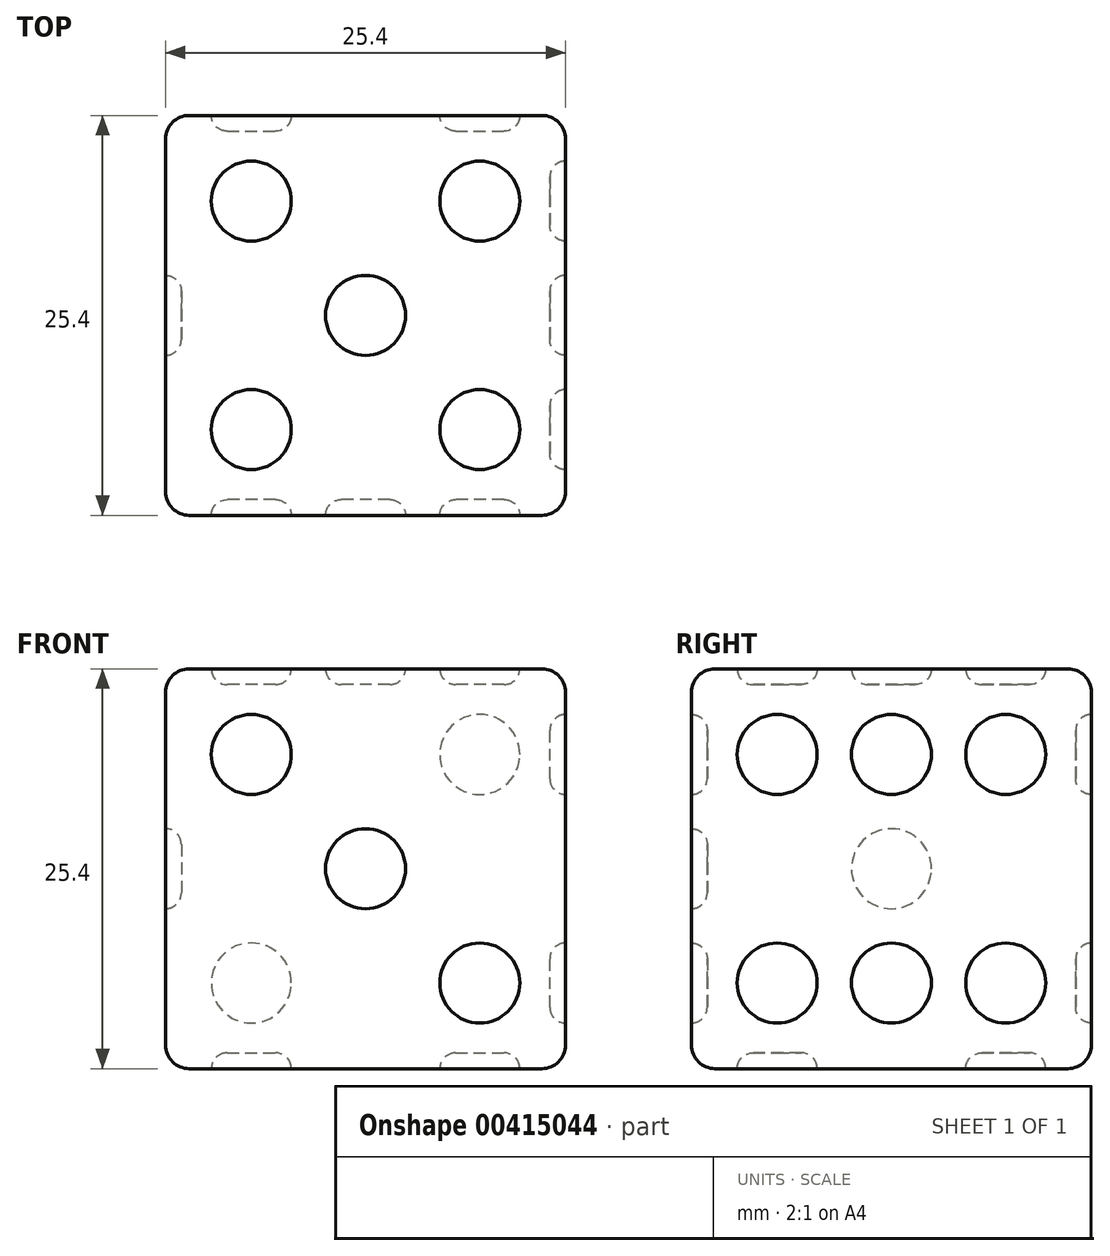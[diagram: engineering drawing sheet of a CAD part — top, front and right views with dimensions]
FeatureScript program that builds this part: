
annotation { "Feature Type Name" : "Feature", "Feature Type Description" : "" }
export const myFeature = defineFeature(function(context is Context, id is Id, definition is map)
    precondition{}
    {
        {
            assignVariable(context, id + "F0", {"name" : "size", "anyValue" : 25.4});
        }
        {
            assignVariable(context, id + "F1", {"name" : "radius", "anyValue" : 1.5});
        }
        {
            var Q0;
            Q0=qCreatedBy(makeId("Top.planeOp"),FACE);
            var sketch = newSketch(context, id + "F2", { "sketchPlane" : qUnion([Q0])});
            skLineSegment(sketch, "E0.bottom", {"start": v(12.7, -12.7) * mm, "end": v(-12.7, -12.7) * mm});
            skLineSegment(sketch, "E0.top", {"start": v(12.7, 12.7) * mm, "end": v(-12.7, 12.7) * mm});
            skLineSegment(sketch, "E0.left", {"start": v(12.7, -12.7) * mm, "end": v(12.7, 12.7) * mm});
            skLineSegment(sketch, "E0.right", {"start": v(-12.7, -12.7) * mm, "end": v(-12.7, 12.7) * mm});
            skPoint(sketch, "E0.middle", {"position": v(0, 0) * mm});
            skSolve(sketch);
        }
        {
            var Q0;
            Q0=makeQuery(id+"F2.imprint","IMPRINT",FACE,{"disambiguationData":[TD([[makeQuery(id+"F2.imprint","IMPRINT",EDGE,{"derivedFrom":sQuery(id+"F2.wireOp",EDGE,"E0.bottom")}),-1.0]])]});
            extrude(context, id + "F3", {"entities" : qUnion([Q0]), "depth" : (getVariable(context, 'size')) * mm});
        }
        {
            var Q0;
            Q0=makeQuery(id+"F3.opExtrude","CAP_FACE",FACE,{"disambiguationData":[OSD([sQuery(id+"F2.wireOp",EDGE,"E0.bottom"),sQuery(id+"F2.wireOp",EDGE,"E0.top"),sQuery(id+"F2.wireOp",EDGE,"E0.left"),sQuery(id+"F2.wireOp",EDGE,"E0.right")])],"isStart":true});
            var sketch = newSketch(context, id + "F4", { "sketchPlane" : qUnion([Q0])});
            skPoint(sketch, "E1", {"position": v(0, 0) * mm});
            skPoint(sketch, "E2", {"position": v(0, 7.26) * mm});
            skPoint(sketch, "E3", {"position": v(7.26, 7.26) * mm});
            skPoint(sketch, "E4", {"position": v(7.26, 0) * mm});
            skPoint(sketch, "E5", {"position": v(7.26, -7.26) * mm});
            skPoint(sketch, "E6", {"position": v(0, -7.26) * mm});
            skPoint(sketch, "E7", {"position": v(-7.26, -7.26) * mm});
            skPoint(sketch, "E8", {"position": v(-7.26, 0) * mm});
            skPoint(sketch, "E9", {"position": v(-7.26, 7.26) * mm});
            skLineSegment(sketch, "E10", {"start": v(-7.26, 7.26) * mm, "end": v(0, 7.26) * mm, "construction": true});
            skLineSegment(sketch, "E11", {"start": v(7.26, 7.26) * mm, "end": v(7.26, 0) * mm, "construction": true});
            skLineSegment(sketch, "E12", {"start": v(7.26, 0) * mm, "end": v(7.26, -7.26) * mm, "construction": true});
            skLineSegment(sketch, "E13", {"start": v(7.26, -7.26) * mm, "end": v(0, -7.26) * mm, "construction": true});
            skLineSegment(sketch, "E14", {"start": v(0, -7.26) * mm, "end": v(-7.26, -7.26) * mm, "construction": true});
            skLineSegment(sketch, "E15", {"start": v(-7.26, 0) * mm, "end": v(-7.26, -7.26) * mm, "construction": true});
            skLineSegment(sketch, "E16", {"start": v(-7.26, 0) * mm, "end": v(-7.26, 7.26) * mm, "construction": true});
            skLineSegment(sketch, "E17", {"start": v(0, 7.26) * mm, "end": v(7.26, 7.26) * mm, "construction": true});
            skLineSegment(sketch, "E18", {"start": v(0, 7.26) * mm, "end": v(0, 0) * mm, "construction": true});
            skLineSegment(sketch, "E19", {"start": v(0, 0) * mm, "end": v(0, -7.26) * mm, "construction": true});
            skLineSegment(sketch, "E20", {"start": v(0, 0) * mm, "end": v(7.26, 0) * mm, "construction": true});
            skLineSegment(sketch, "E21", {"start": v(0, 0) * mm, "end": v(-7.26, 0) * mm, "construction": true});
            skCircle(sketch, "E22", {"center": v(-7.26, 7.26) * mm, "radius": 2.54 * mm});
            skCircle(sketch, "E23", {"center": v(-7.26, 0) * mm, "radius": 2.54 * mm});
            skCircle(sketch, "E24", {"center": v(-7.26, -7.26) * mm, "radius": 2.54 * mm});
            skCircle(sketch, "E25", {"center": v(0, -7.26) * mm, "radius": 2.54 * mm});
            skCircle(sketch, "E26", {"center": v(7.26, -7.26) * mm, "radius": 2.54 * mm});
            skCircle(sketch, "E27", {"center": v(7.26, 0) * mm, "radius": 2.54 * mm});
            skCircle(sketch, "E28", {"center": v(7.26, 7.26) * mm, "radius": 2.54 * mm});
            skCircle(sketch, "E29", {"center": v(0, 0) * mm, "radius": 2.54 * mm});
            skCircle(sketch, "E30", {"center": v(0, 7.26) * mm, "radius": 2.54 * mm});
            skSolve(sketch);
        }
        {
            var Q0;
            Q0=makeQuery(id+"F3.opExtrude","CAP_FACE",FACE,{"disambiguationData":[OSD([sQuery(id+"F2.wireOp",EDGE,"E0.bottom"),sQuery(id+"F2.wireOp",EDGE,"E0.top"),sQuery(id+"F2.wireOp",EDGE,"E0.left"),sQuery(id+"F2.wireOp",EDGE,"E0.right")])],"isStart":false});
            var sketch = newSketch(context, id + "F5", { "sketchPlane" : qUnion([Q0])});
            skPoint(sketch, "E31", {"position": v(0, 0) * mm});
            skPoint(sketch, "E32", {"position": v(0, 7.26) * mm});
            skPoint(sketch, "E33", {"position": v(7.26, 7.26) * mm});
            skPoint(sketch, "E34", {"position": v(7.26, 0) * mm});
            skPoint(sketch, "E35", {"position": v(7.26, -7.26) * mm});
            skPoint(sketch, "E36", {"position": v(0, -7.26) * mm});
            skPoint(sketch, "E37", {"position": v(-7.26, -7.26) * mm});
            skPoint(sketch, "E38", {"position": v(-7.26, 0) * mm});
            skPoint(sketch, "E39", {"position": v(-7.26, 7.26) * mm});
            skLineSegment(sketch, "E40", {"start": v(-7.26, 7.26) * mm, "end": v(0, 7.26) * mm, "construction": true});
            skLineSegment(sketch, "E41", {"start": v(7.26, 7.26) * mm, "end": v(7.26, 0) * mm, "construction": true});
            skLineSegment(sketch, "E42", {"start": v(7.26, 0) * mm, "end": v(7.26, -7.26) * mm, "construction": true});
            skLineSegment(sketch, "E43", {"start": v(7.26, -7.26) * mm, "end": v(0, -7.26) * mm, "construction": true});
            skLineSegment(sketch, "E44", {"start": v(0, -7.26) * mm, "end": v(-7.26, -7.26) * mm, "construction": true});
            skLineSegment(sketch, "E45", {"start": v(-7.26, 0) * mm, "end": v(-7.26, -7.26) * mm, "construction": true});
            skLineSegment(sketch, "E46", {"start": v(-7.26, 0) * mm, "end": v(-7.26, 7.26) * mm, "construction": true});
            skLineSegment(sketch, "E47", {"start": v(0, 7.26) * mm, "end": v(7.26, 7.26) * mm, "construction": true});
            skLineSegment(sketch, "E48", {"start": v(0, 7.26) * mm, "end": v(0, 0) * mm, "construction": true});
            skLineSegment(sketch, "E49", {"start": v(0, 0) * mm, "end": v(0, -7.26) * mm, "construction": true});
            skLineSegment(sketch, "E50", {"start": v(0, 0) * mm, "end": v(7.26, 0) * mm, "construction": true});
            skLineSegment(sketch, "E51", {"start": v(0, 0) * mm, "end": v(-7.26, 0) * mm, "construction": true});
            skCircle(sketch, "E52", {"center": v(-7.26, 7.26) * mm, "radius": 2.54 * mm});
            skCircle(sketch, "E53", {"center": v(-7.26, 0) * mm, "radius": 2.54 * mm});
            skCircle(sketch, "E54", {"center": v(-7.26, -7.26) * mm, "radius": 2.54 * mm});
            skCircle(sketch, "E55", {"center": v(0, -7.26) * mm, "radius": 2.54 * mm});
            skCircle(sketch, "E56", {"center": v(7.26, -7.26) * mm, "radius": 2.54 * mm});
            skCircle(sketch, "E57", {"center": v(7.26, 0) * mm, "radius": 2.54 * mm});
            skCircle(sketch, "E58", {"center": v(7.26, 7.26) * mm, "radius": 2.54 * mm});
            skCircle(sketch, "E59", {"center": v(0, 0) * mm, "radius": 2.54 * mm});
            skCircle(sketch, "E60", {"center": v(0, 7.26) * mm, "radius": 2.54 * mm});
            skSolve(sketch);
        }
        {
            var Q0;
            Q0=makeQuery(id+"F3.opExtrude","SWEPT_FACE",FACE,{"disambiguationData":[OSD([sQuery(id+"F2.wireOp",EDGE,"E0.left")])]});
            var sketch = newSketch(context, id + "F6", { "sketchPlane" : qUnion([Q0])});
            skPoint(sketch, "E61", {"position": v(0, 12.7) * mm});
            skPoint(sketch, "E62", {"position": v(0, 19.96) * mm});
            skPoint(sketch, "E63", {"position": v(7.26, 19.96) * mm});
            skPoint(sketch, "E64", {"position": v(7.26, 12.7) * mm});
            skPoint(sketch, "E65", {"position": v(7.26, 5.44) * mm});
            skPoint(sketch, "E66", {"position": v(0, 5.44) * mm});
            skPoint(sketch, "E67", {"position": v(-7.26, 5.44) * mm});
            skPoint(sketch, "E68", {"position": v(-7.26, 12.7) * mm});
            skPoint(sketch, "E69", {"position": v(-7.26, 19.96) * mm});
            skLineSegment(sketch, "E70", {"start": v(-7.26, 19.96) * mm, "end": v(0, 19.96) * mm, "construction": true});
            skLineSegment(sketch, "E71", {"start": v(7.26, 19.96) * mm, "end": v(7.26, 12.7) * mm, "construction": true});
            skLineSegment(sketch, "E72", {"start": v(7.26, 12.7) * mm, "end": v(7.26, 5.44) * mm, "construction": true});
            skLineSegment(sketch, "E73", {"start": v(7.26, 5.44) * mm, "end": v(0, 5.44) * mm, "construction": true});
            skLineSegment(sketch, "E74", {"start": v(0, 5.44) * mm, "end": v(-7.26, 5.44) * mm, "construction": true});
            skLineSegment(sketch, "E75", {"start": v(-7.26, 12.7) * mm, "end": v(-7.26, 5.44) * mm, "construction": true});
            skLineSegment(sketch, "E76", {"start": v(-7.26, 12.7) * mm, "end": v(-7.26, 19.96) * mm, "construction": true});
            skLineSegment(sketch, "E77", {"start": v(0, 19.96) * mm, "end": v(7.26, 19.96) * mm, "construction": true});
            skLineSegment(sketch, "E78", {"start": v(0, 19.96) * mm, "end": v(0, 12.7) * mm, "construction": true});
            skLineSegment(sketch, "E79", {"start": v(0, 12.7) * mm, "end": v(0, 5.44) * mm, "construction": true});
            skLineSegment(sketch, "E80", {"start": v(0, 12.7) * mm, "end": v(7.26, 12.7) * mm, "construction": true});
            skLineSegment(sketch, "E81", {"start": v(0, 12.7) * mm, "end": v(-7.26, 12.7) * mm, "construction": true});
            skCircle(sketch, "E82", {"center": v(-7.26, 19.96) * mm, "radius": 2.54 * mm});
            skCircle(sketch, "E83", {"center": v(-7.26, 12.7) * mm, "radius": 2.54 * mm});
            skCircle(sketch, "E84", {"center": v(-7.26, 5.44) * mm, "radius": 2.54 * mm});
            skCircle(sketch, "E85", {"center": v(0, 5.44) * mm, "radius": 2.54 * mm});
            skCircle(sketch, "E86", {"center": v(7.26, 5.44) * mm, "radius": 2.54 * mm});
            skCircle(sketch, "E87", {"center": v(7.26, 12.7) * mm, "radius": 2.54 * mm});
            skCircle(sketch, "E88", {"center": v(7.26, 19.96) * mm, "radius": 2.54 * mm});
            skCircle(sketch, "E89", {"center": v(0, 12.7) * mm, "radius": 2.54 * mm});
            skCircle(sketch, "E90", {"center": v(0, 19.96) * mm, "radius": 2.54 * mm});
            skLineSegment(sketch, "E91", {"start": v(0, 25.4) * mm, "end": v(0, 0) * mm, "construction": true});
            skSolve(sketch);
        }
        {
            var Q0;
            Q0=makeQuery(id+"F3.opExtrude","SWEPT_FACE",FACE,{"disambiguationData":[OSD([sQuery(id+"F2.wireOp",EDGE,"E0.top")])]});
            var sketch = newSketch(context, id + "F7", { "sketchPlane" : qUnion([Q0])});
            skPoint(sketch, "E92", {"position": v(0, 12.7) * mm});
            skPoint(sketch, "E93", {"position": v(0, 19.96) * mm});
            skPoint(sketch, "E94", {"position": v(7.26, 19.96) * mm});
            skPoint(sketch, "E95", {"position": v(7.26, 12.7) * mm});
            skPoint(sketch, "E96", {"position": v(7.26, 5.44) * mm});
            skPoint(sketch, "E97", {"position": v(0, 5.44) * mm});
            skPoint(sketch, "E98", {"position": v(-7.26, 5.44) * mm});
            skPoint(sketch, "E99", {"position": v(-7.26, 12.7) * mm});
            skPoint(sketch, "E100", {"position": v(-7.26, 19.96) * mm});
            skLineSegment(sketch, "E101", {"start": v(-7.26, 19.96) * mm, "end": v(0, 19.96) * mm, "construction": true});
            skLineSegment(sketch, "E102", {"start": v(7.26, 19.96) * mm, "end": v(7.26, 12.7) * mm, "construction": true});
            skLineSegment(sketch, "E103", {"start": v(7.26, 12.7) * mm, "end": v(7.26, 5.44) * mm, "construction": true});
            skLineSegment(sketch, "E104", {"start": v(7.26, 5.44) * mm, "end": v(0, 5.44) * mm, "construction": true});
            skLineSegment(sketch, "E105", {"start": v(0, 5.44) * mm, "end": v(-7.26, 5.44) * mm, "construction": true});
            skLineSegment(sketch, "E106", {"start": v(-7.26, 12.7) * mm, "end": v(-7.26, 5.44) * mm, "construction": true});
            skLineSegment(sketch, "E107", {"start": v(-7.26, 12.7) * mm, "end": v(-7.26, 19.96) * mm, "construction": true});
            skLineSegment(sketch, "E108", {"start": v(0, 19.96) * mm, "end": v(7.26, 19.96) * mm, "construction": true});
            skLineSegment(sketch, "E109", {"start": v(0, 19.96) * mm, "end": v(0, 12.7) * mm, "construction": true});
            skLineSegment(sketch, "E110", {"start": v(0, 12.7) * mm, "end": v(0, 5.44) * mm, "construction": true});
            skLineSegment(sketch, "E111", {"start": v(0, 12.7) * mm, "end": v(7.26, 12.7) * mm, "construction": true});
            skLineSegment(sketch, "E112", {"start": v(0, 12.7) * mm, "end": v(-7.26, 12.7) * mm, "construction": true});
            skCircle(sketch, "E113", {"center": v(-7.26, 19.96) * mm, "radius": 2.54 * mm});
            skCircle(sketch, "E114", {"center": v(-7.26, 12.7) * mm, "radius": 2.54 * mm});
            skCircle(sketch, "E115", {"center": v(-7.26, 5.44) * mm, "radius": 2.54 * mm});
            skCircle(sketch, "E116", {"center": v(0, 5.44) * mm, "radius": 2.54 * mm});
            skCircle(sketch, "E117", {"center": v(7.26, 5.44) * mm, "radius": 2.54 * mm});
            skCircle(sketch, "E118", {"center": v(7.26, 12.7) * mm, "radius": 2.54 * mm});
            skCircle(sketch, "E119", {"center": v(7.26, 19.96) * mm, "radius": 2.54 * mm});
            skCircle(sketch, "E120", {"center": v(0, 12.7) * mm, "radius": 2.54 * mm});
            skCircle(sketch, "E121", {"center": v(0, 19.96) * mm, "radius": 2.54 * mm});
            skLineSegment(sketch, "E122", {"start": v(0, 25.4) * mm, "end": v(0, 0) * mm, "construction": true});
            skSolve(sketch);
        }
        {
            var Q0;
            Q0=makeQuery(id+"F3.opExtrude","SWEPT_FACE",FACE,{"disambiguationData":[OSD([sQuery(id+"F2.wireOp",EDGE,"E0.right")])]});
            var sketch = newSketch(context, id + "F8", { "sketchPlane" : qUnion([Q0])});
            skLineSegment(sketch, "E123", {"start": v(0, 25.4) * mm, "end": v(0, 0) * mm, "construction": true});
            skPoint(sketch, "E124", {"position": v(0, 12.7) * mm});
            skPoint(sketch, "E125", {"position": v(0, 19.96) * mm});
            skPoint(sketch, "E126", {"position": v(7.26, 19.96) * mm});
            skPoint(sketch, "E127", {"position": v(7.26, 12.7) * mm});
            skPoint(sketch, "E128", {"position": v(7.26, 5.44) * mm});
            skPoint(sketch, "E129", {"position": v(0, 5.44) * mm});
            skPoint(sketch, "E130", {"position": v(-7.26, 5.44) * mm});
            skPoint(sketch, "E131", {"position": v(-7.26, 12.7) * mm});
            skPoint(sketch, "E132", {"position": v(-7.26, 19.96) * mm});
            skLineSegment(sketch, "E133", {"start": v(-7.26, 19.96) * mm, "end": v(0, 19.96) * mm, "construction": true});
            skLineSegment(sketch, "E134", {"start": v(7.26, 19.96) * mm, "end": v(7.26, 12.7) * mm, "construction": true});
            skLineSegment(sketch, "E135", {"start": v(7.26, 12.7) * mm, "end": v(7.26, 5.44) * mm, "construction": true});
            skLineSegment(sketch, "E136", {"start": v(7.26, 5.44) * mm, "end": v(0, 5.44) * mm, "construction": true});
            skLineSegment(sketch, "E137", {"start": v(0, 5.44) * mm, "end": v(-7.26, 5.44) * mm, "construction": true});
            skLineSegment(sketch, "E138", {"start": v(-7.26, 12.7) * mm, "end": v(-7.26, 5.44) * mm, "construction": true});
            skLineSegment(sketch, "E139", {"start": v(-7.26, 12.7) * mm, "end": v(-7.26, 19.96) * mm, "construction": true});
            skLineSegment(sketch, "E140", {"start": v(0, 19.96) * mm, "end": v(7.26, 19.96) * mm, "construction": true});
            skLineSegment(sketch, "E141", {"start": v(0, 19.96) * mm, "end": v(0, 12.7) * mm, "construction": true});
            skLineSegment(sketch, "E142", {"start": v(0, 12.7) * mm, "end": v(0, 5.44) * mm, "construction": true});
            skLineSegment(sketch, "E143", {"start": v(0, 12.7) * mm, "end": v(7.26, 12.7) * mm, "construction": true});
            skLineSegment(sketch, "E144", {"start": v(0, 12.7) * mm, "end": v(-7.26, 12.7) * mm, "construction": true});
            skCircle(sketch, "E145", {"center": v(-7.26, 19.96) * mm, "radius": 2.54 * mm});
            skCircle(sketch, "E146", {"center": v(-7.26, 12.7) * mm, "radius": 2.54 * mm});
            skCircle(sketch, "E147", {"center": v(-7.26, 5.44) * mm, "radius": 2.54 * mm});
            skCircle(sketch, "E148", {"center": v(0, 5.44) * mm, "radius": 2.54 * mm});
            skCircle(sketch, "E149", {"center": v(7.26, 5.44) * mm, "radius": 2.54 * mm});
            skCircle(sketch, "E150", {"center": v(7.26, 12.7) * mm, "radius": 2.54 * mm});
            skCircle(sketch, "E151", {"center": v(7.26, 19.96) * mm, "radius": 2.54 * mm});
            skCircle(sketch, "E152", {"center": v(0, 12.7) * mm, "radius": 2.54 * mm});
            skCircle(sketch, "E153", {"center": v(0, 19.96) * mm, "radius": 2.54 * mm});
            skSolve(sketch);
        }
        {
            var Q0;
            Q0=makeQuery(id+"F3.opExtrude","SWEPT_FACE",FACE,{"disambiguationData":[OSD([sQuery(id+"F2.wireOp",EDGE,"E0.bottom")])]});
            var sketch = newSketch(context, id + "F9", { "sketchPlane" : qUnion([Q0])});
            skLineSegment(sketch, "E154", {"start": v(0, 25.4) * mm, "end": v(0, 0) * mm, "construction": true});
            skPoint(sketch, "E155", {"position": v(0, 12.7) * mm});
            skPoint(sketch, "E156", {"position": v(0, 19.96) * mm});
            skPoint(sketch, "E157", {"position": v(7.26, 19.96) * mm});
            skPoint(sketch, "E158", {"position": v(7.26, 12.7) * mm});
            skPoint(sketch, "E159", {"position": v(7.26, 5.44) * mm});
            skPoint(sketch, "E160", {"position": v(0, 5.44) * mm});
            skPoint(sketch, "E161", {"position": v(-7.26, 5.44) * mm});
            skPoint(sketch, "E162", {"position": v(-7.26, 12.7) * mm});
            skPoint(sketch, "E163", {"position": v(-7.26, 19.96) * mm});
            skLineSegment(sketch, "E164", {"start": v(-7.26, 19.96) * mm, "end": v(0, 19.96) * mm, "construction": true});
            skLineSegment(sketch, "E165", {"start": v(7.26, 19.96) * mm, "end": v(7.26, 12.7) * mm, "construction": true});
            skLineSegment(sketch, "E166", {"start": v(7.26, 12.7) * mm, "end": v(7.26, 5.44) * mm, "construction": true});
            skLineSegment(sketch, "E167", {"start": v(7.26, 5.44) * mm, "end": v(0, 5.44) * mm, "construction": true});
            skLineSegment(sketch, "E168", {"start": v(0, 5.44) * mm, "end": v(-7.26, 5.44) * mm, "construction": true});
            skLineSegment(sketch, "E169", {"start": v(-7.26, 12.7) * mm, "end": v(-7.26, 5.44) * mm, "construction": true});
            skLineSegment(sketch, "E170", {"start": v(-7.26, 12.7) * mm, "end": v(-7.26, 19.96) * mm, "construction": true});
            skLineSegment(sketch, "E171", {"start": v(0, 19.96) * mm, "end": v(7.26, 19.96) * mm, "construction": true});
            skLineSegment(sketch, "E172", {"start": v(0, 19.96) * mm, "end": v(0, 12.7) * mm, "construction": true});
            skLineSegment(sketch, "E173", {"start": v(0, 12.7) * mm, "end": v(0, 5.44) * mm, "construction": true});
            skLineSegment(sketch, "E174", {"start": v(0, 12.7) * mm, "end": v(7.26, 12.7) * mm, "construction": true});
            skLineSegment(sketch, "E175", {"start": v(0, 12.7) * mm, "end": v(-7.26, 12.7) * mm, "construction": true});
            skCircle(sketch, "E176", {"center": v(-7.26, 19.96) * mm, "radius": 2.54 * mm});
            skCircle(sketch, "E177", {"center": v(-7.26, 12.7) * mm, "radius": 2.54 * mm});
            skCircle(sketch, "E178", {"center": v(-7.26, 5.44) * mm, "radius": 2.54 * mm});
            skCircle(sketch, "E179", {"center": v(0, 5.44) * mm, "radius": 2.54 * mm});
            skCircle(sketch, "E180", {"center": v(7.26, 5.44) * mm, "radius": 2.54 * mm});
            skCircle(sketch, "E181", {"center": v(7.26, 12.7) * mm, "radius": 2.54 * mm});
            skCircle(sketch, "E182", {"center": v(7.26, 19.96) * mm, "radius": 2.54 * mm});
            skCircle(sketch, "E183", {"center": v(0, 12.7) * mm, "radius": 2.54 * mm});
            skCircle(sketch, "E184", {"center": v(0, 19.96) * mm, "radius": 2.54 * mm});
            skSolve(sketch);
        }
        {
            var Q0;
            Q0=makeQuery(id+"F4.imprint","IMPRINT",FACE,{"disambiguationData":[TD([[makeQuery(id+"F4.imprint","IMPRINT",EDGE,{"derivedFrom":sQuery(id+"F4.wireOp",EDGE,"E28")}),1.0]])]});
            var Q1;
            Q1=makeQuery(id+"F4.imprint","IMPRINT",FACE,{"disambiguationData":[TD([[makeQuery(id+"F4.imprint","IMPRINT",EDGE,{"derivedFrom":sQuery(id+"F4.wireOp",EDGE,"E27")}),1.0]])]});
            var Q2;
            Q2=makeQuery(id+"F4.imprint","IMPRINT",FACE,{"disambiguationData":[TD([[makeQuery(id+"F4.imprint","IMPRINT",EDGE,{"derivedFrom":sQuery(id+"F4.wireOp",EDGE,"E26")}),1.0]])]});
            var Q3;
            Q3=makeQuery(id+"F4.imprint","IMPRINT",FACE,{"disambiguationData":[TD([[makeQuery(id+"F4.imprint","IMPRINT",EDGE,{"derivedFrom":sQuery(id+"F4.wireOp",EDGE,"E24")}),1.0]])]});
            var Q4;
            Q4=makeQuery(id+"F4.imprint","IMPRINT",FACE,{"disambiguationData":[TD([[makeQuery(id+"F4.imprint","IMPRINT",EDGE,{"derivedFrom":sQuery(id+"F4.wireOp",EDGE,"E23")}),1.0]])]});
            var Q5;
            Q5=makeQuery(id+"F4.imprint","IMPRINT",FACE,{"disambiguationData":[TD([[makeQuery(id+"F4.imprint","IMPRINT",EDGE,{"derivedFrom":sQuery(id+"F4.wireOp",EDGE,"E22")}),1.0]])]});
            extrude(context, id + "F10", {"entities" : qUnion([Q0, Q1, Q2, Q3, Q4, Q5]), "operationType" : NewBodyOperationType.REMOVE, "oppositeDirection" : true, "depth" : 1 * mm});
        }
        {
            var Q0;
            Q0=makeQuery(id+"F10.boolean.opBoolean","COPY",EDGE,{"derivedFrom":makeQuery(id+"F10.opExtrude","CAP_EDGE",EDGE,{"disambiguationData":[OSD([sQuery(id+"F4.wireOp",EDGE,"E26")])],"isStart":false})});
            var Q1;
            Q1=makeQuery(id+"F10.boolean.opBoolean","COPY",EDGE,{"derivedFrom":makeQuery(id+"F10.opExtrude","CAP_EDGE",EDGE,{"disambiguationData":[OSD([sQuery(id+"F4.wireOp",EDGE,"E24")])],"isStart":false})});
            var Q2;
            Q2=makeQuery(id+"F10.boolean.opBoolean","COPY",EDGE,{"derivedFrom":makeQuery(id+"F10.opExtrude","CAP_EDGE",EDGE,{"disambiguationData":[OSD([sQuery(id+"F4.wireOp",EDGE,"E27")])],"isStart":false})});
            var Q3;
            Q3=makeQuery(id+"F10.boolean.opBoolean","COPY",EDGE,{"derivedFrom":makeQuery(id+"F10.opExtrude","CAP_EDGE",EDGE,{"disambiguationData":[OSD([sQuery(id+"F4.wireOp",EDGE,"E28")])],"isStart":false})});
            var Q4;
            Q4=makeQuery(id+"F10.boolean.opBoolean","COPY",EDGE,{"derivedFrom":makeQuery(id+"F10.opExtrude","CAP_EDGE",EDGE,{"disambiguationData":[OSD([sQuery(id+"F4.wireOp",EDGE,"E23")])],"isStart":false})});
            var Q5;
            Q5=makeQuery(id+"F10.boolean.opBoolean","COPY",EDGE,{"derivedFrom":makeQuery(id+"F10.opExtrude","CAP_EDGE",EDGE,{"disambiguationData":[OSD([sQuery(id+"F4.wireOp",EDGE,"E22")])],"isStart":false})});
            fillet(context, id + "F11", {"entities" : qUnion([Q0, Q1, Q2, Q3, Q4, Q5]), "radius" : 1 * mm, "tangentPropagation" : true, "allowEdgeOverflow" : false});
        }
        {
            var Q0;
            Q0=makeQuery(id+"F5.imprint","IMPRINT",FACE,{"disambiguationData":[TD([[makeQuery(id+"F5.imprint","IMPRINT",EDGE,{"derivedFrom":sQuery(id+"F5.wireOp",EDGE,"E59")}),1.0]])]});
            var Q1;
            Q1=sQuery(id+"F5.wireOp",EDGE,"E59");
            extrude(context, id + "F12", {"entities" : qUnion([Q0]), "operationType" : NewBodyOperationType.REMOVE, "surfaceEntities" : qUnion([Q1]), "oppositeDirection" : true, "depth" : 1 * mm});
        }
        {
            var Q0;
            Q0=makeQuery(id+"F12.boolean.opBoolean","COPY",EDGE,{"derivedFrom":makeQuery(id+"F12.opExtrude","CAP_EDGE",EDGE,{"disambiguationData":[OSD([sQuery(id+"F5.wireOp",EDGE,"E59")])],"isStart":false})});
            fillet(context, id + "F13", {"entities" : qUnion([Q0]), "radius" : 1 * mm, "tangentPropagation" : true, "allowEdgeOverflow" : false});
        }
        {
            var Q0;
            Q0=makeQuery(id+"F9.imprint","IMPRINT",FACE,{"disambiguationData":[TD([[makeQuery(id+"F9.imprint","IMPRINT",EDGE,{"derivedFrom":sQuery(id+"F9.wireOp",EDGE,"E182")}),1.0]])]});
            var Q1;
            Q1=makeQuery(id+"F9.imprint","IMPRINT",FACE,{"disambiguationData":[TD([[makeQuery(id+"F9.imprint","IMPRINT",EDGE,{"derivedFrom":sQuery(id+"F9.wireOp",EDGE,"E183")}),1.0]])]});
            var Q2;
            Q2=makeQuery(id+"F9.imprint","IMPRINT",FACE,{"disambiguationData":[TD([[makeQuery(id+"F9.imprint","IMPRINT",EDGE,{"derivedFrom":sQuery(id+"F9.wireOp",EDGE,"E178")}),1.0]])]});
            var Q3;
            Q3=sQuery(id+"F9.wireOp",EDGE,"E182");
            var Q4;
            Q4=sQuery(id+"F9.wireOp",EDGE,"E183");
            var Q5;
            Q5=sQuery(id+"F9.wireOp",EDGE,"E178");
            extrude(context, id + "F14", {"entities" : qUnion([Q0, Q1, Q2]), "operationType" : NewBodyOperationType.REMOVE, "surfaceEntities" : qUnion([Q3, Q4, Q5]), "oppositeDirection" : true, "depth" : 1 * mm});
        }
        {
            var Q0;
            Q0=makeQuery(id+"F14.boolean.opBoolean","COPY",EDGE,{"derivedFrom":makeQuery(id+"F14.opExtrude","CAP_EDGE",EDGE,{"disambiguationData":[OSD([sQuery(id+"F9.wireOp",EDGE,"E182")])],"isStart":false})});
            var Q1;
            Q1=makeQuery(id+"F14.boolean.opBoolean","COPY",EDGE,{"derivedFrom":makeQuery(id+"F14.opExtrude","CAP_EDGE",EDGE,{"disambiguationData":[OSD([sQuery(id+"F9.wireOp",EDGE,"E183")])],"isStart":false})});
            var Q2;
            Q2=makeQuery(id+"F14.boolean.opBoolean","COPY",EDGE,{"derivedFrom":makeQuery(id+"F14.opExtrude","CAP_EDGE",EDGE,{"disambiguationData":[OSD([sQuery(id+"F9.wireOp",EDGE,"E178")])],"isStart":false})});
            fillet(context, id + "F15", {"entities" : qUnion([Q0, Q1, Q2]), "radius" : 1 * mm, "tangentPropagation" : true, "allowEdgeOverflow" : false});
        }
        {
            var Q0;
            Q0=makeQuery(id+"F6.imprint","IMPRINT",FACE,{"disambiguationData":[TD([[makeQuery(id+"F6.imprint","IMPRINT",EDGE,{"derivedFrom":sQuery(id+"F6.wireOp",EDGE,"E82")}),1.0]])]});
            var Q1;
            Q1=makeQuery(id+"F6.imprint","IMPRINT",FACE,{"disambiguationData":[TD([[makeQuery(id+"F6.imprint","IMPRINT",EDGE,{"derivedFrom":sQuery(id+"F6.wireOp",EDGE,"E84")}),1.0]])]});
            var Q2;
            Q2=makeQuery(id+"F6.imprint","IMPRINT",FACE,{"disambiguationData":[TD([[makeQuery(id+"F6.imprint","IMPRINT",EDGE,{"derivedFrom":sQuery(id+"F6.wireOp",EDGE,"E88")}),1.0]])]});
            var Q3;
            Q3=makeQuery(id+"F6.imprint","IMPRINT",FACE,{"disambiguationData":[TD([[makeQuery(id+"F6.imprint","IMPRINT",EDGE,{"derivedFrom":sQuery(id+"F6.wireOp",EDGE,"E89")}),1.0]])]});
            var Q4;
            Q4=makeQuery(id+"F6.imprint","IMPRINT",FACE,{"disambiguationData":[TD([[makeQuery(id+"F6.imprint","IMPRINT",EDGE,{"derivedFrom":sQuery(id+"F6.wireOp",EDGE,"E86")}),1.0]])]});
            extrude(context, id + "F16", {"entities" : qUnion([Q0, Q1, Q2, Q3, Q4]), "operationType" : NewBodyOperationType.REMOVE, "oppositeDirection" : true, "depth" : 1 * mm});
        }
        {
            var Q0;
            Q0=makeQuery(id+"F16.boolean.opBoolean","COPY",EDGE,{"derivedFrom":makeQuery(id+"F16.opExtrude","CAP_EDGE",EDGE,{"disambiguationData":[OSD([sQuery(id+"F6.wireOp",EDGE,"E84")])],"isStart":false})});
            var Q1;
            Q1=makeQuery(id+"F16.boolean.opBoolean","COPY",EDGE,{"derivedFrom":makeQuery(id+"F16.opExtrude","CAP_EDGE",EDGE,{"disambiguationData":[OSD([sQuery(id+"F6.wireOp",EDGE,"E82")])],"isStart":false})});
            var Q2;
            Q2=makeQuery(id+"F16.boolean.opBoolean","COPY",EDGE,{"derivedFrom":makeQuery(id+"F16.opExtrude","CAP_EDGE",EDGE,{"disambiguationData":[OSD([sQuery(id+"F6.wireOp",EDGE,"E89")])],"isStart":false})});
            var Q3;
            Q3=makeQuery(id+"F16.boolean.opBoolean","COPY",EDGE,{"derivedFrom":makeQuery(id+"F16.opExtrude","CAP_EDGE",EDGE,{"disambiguationData":[OSD([sQuery(id+"F6.wireOp",EDGE,"E86")])],"isStart":false})});
            var Q4;
            Q4=makeQuery(id+"F16.boolean.opBoolean","COPY",EDGE,{"derivedFrom":makeQuery(id+"F16.opExtrude","CAP_EDGE",EDGE,{"disambiguationData":[OSD([sQuery(id+"F6.wireOp",EDGE,"E88")])],"isStart":false})});
            fillet(context, id + "F17", {"entities" : qUnion([Q0, Q1, Q2, Q3, Q4]), "radius" : 1 * mm, "tangentPropagation" : true, "allowEdgeOverflow" : false});
        }
        {
            var Q0;
            Q0=makeQuery(id+"F7.imprint","IMPRINT",FACE,{"disambiguationData":[TD([[makeQuery(id+"F7.imprint","IMPRINT",EDGE,{"derivedFrom":sQuery(id+"F7.wireOp",EDGE,"E113")}),1.0]])]});
            var Q1;
            Q1=makeQuery(id+"F7.imprint","IMPRINT",FACE,{"disambiguationData":[TD([[makeQuery(id+"F7.imprint","IMPRINT",EDGE,{"derivedFrom":sQuery(id+"F7.wireOp",EDGE,"E115")}),1.0]])]});
            var Q2;
            Q2=makeQuery(id+"F7.imprint","IMPRINT",FACE,{"disambiguationData":[TD([[makeQuery(id+"F7.imprint","IMPRINT",EDGE,{"derivedFrom":sQuery(id+"F7.wireOp",EDGE,"E119")}),1.0]])]});
            var Q3;
            Q3=makeQuery(id+"F7.imprint","IMPRINT",FACE,{"disambiguationData":[TD([[makeQuery(id+"F7.imprint","IMPRINT",EDGE,{"derivedFrom":sQuery(id+"F7.wireOp",EDGE,"E117")}),1.0]])]});
            extrude(context, id + "F18", {"entities" : qUnion([Q0, Q1, Q2, Q3]), "operationType" : NewBodyOperationType.REMOVE, "oppositeDirection" : true, "depth" : 1 * mm});
        }
        {
            var Q0;
            Q0=makeQuery(id+"F18.boolean.opBoolean","COPY",EDGE,{"derivedFrom":makeQuery(id+"F18.opExtrude","CAP_EDGE",EDGE,{"disambiguationData":[OSD([sQuery(id+"F7.wireOp",EDGE,"E115")])],"isStart":false})});
            var Q1;
            Q1=makeQuery(id+"F18.boolean.opBoolean","COPY",EDGE,{"derivedFrom":makeQuery(id+"F18.opExtrude","CAP_EDGE",EDGE,{"disambiguationData":[OSD([sQuery(id+"F7.wireOp",EDGE,"E113")])],"isStart":false})});
            var Q2;
            Q2=makeQuery(id+"F18.boolean.opBoolean","COPY",EDGE,{"derivedFrom":makeQuery(id+"F18.opExtrude","CAP_EDGE",EDGE,{"disambiguationData":[OSD([sQuery(id+"F7.wireOp",EDGE,"E119")])],"isStart":false})});
            var Q3;
            Q3=makeQuery(id+"F18.boolean.opBoolean","COPY",EDGE,{"derivedFrom":makeQuery(id+"F18.opExtrude","CAP_EDGE",EDGE,{"disambiguationData":[OSD([sQuery(id+"F7.wireOp",EDGE,"E117")])],"isStart":false})});
            fillet(context, id + "F19", {"entities" : qUnion([Q0, Q1, Q2, Q3]), "radius" : 1 * mm, "tangentPropagation" : true, "allowEdgeOverflow" : false});
        }
        {
            var Q0;
            Q0=makeQuery(id+"F8.imprint","IMPRINT",FACE,{"disambiguationData":[TD([[makeQuery(id+"F8.imprint","IMPRINT",EDGE,{"derivedFrom":sQuery(id+"F8.wireOp",EDGE,"E149")}),1.0]])]});
            var Q1;
            Q1=makeQuery(id+"F8.imprint","IMPRINT",FACE,{"disambiguationData":[TD([[makeQuery(id+"F8.imprint","IMPRINT",EDGE,{"derivedFrom":sQuery(id+"F8.wireOp",EDGE,"E145")}),1.0]])]});
            extrude(context, id + "F20", {"entities" : qUnion([Q0, Q1]), "operationType" : NewBodyOperationType.REMOVE, "oppositeDirection" : true, "depth" : 1 * mm});
        }
        {
            var Q0;
            Q0=makeQuery(id+"F20.boolean.opBoolean","COPY",EDGE,{"derivedFrom":makeQuery(id+"F20.opExtrude","CAP_EDGE",EDGE,{"disambiguationData":[OSD([sQuery(id+"F8.wireOp",EDGE,"E145")])],"isStart":false})});
            var Q1;
            Q1=makeQuery(id+"F20.boolean.opBoolean","COPY",EDGE,{"derivedFrom":makeQuery(id+"F20.opExtrude","CAP_EDGE",EDGE,{"disambiguationData":[OSD([sQuery(id+"F8.wireOp",EDGE,"E149")])],"isStart":false})});
            fillet(context, id + "F21", {"entities" : qUnion([Q0, Q1]), "radius" : 1 * mm, "tangentPropagation" : true, "allowEdgeOverflow" : false});
        }
        {
            var Q0;
            Q0=makeQuery(id+"F3.opExtrude","CAP_EDGE",EDGE,{"disambiguationData":[OSD([sQuery(id+"F2.wireOp",EDGE,"E0.bottom")])],"isStart":false});
            var Q1;
            Q1=makeQuery(id+"F3.opExtrude","CAP_EDGE",EDGE,{"disambiguationData":[OSD([sQuery(id+"F2.wireOp",EDGE,"E0.left")])],"isStart":false});
            var Q2;
            Q2=makeQuery(id+"F3.opExtrude","CAP_EDGE",EDGE,{"disambiguationData":[OSD([sQuery(id+"F2.wireOp",EDGE,"E0.top")])],"isStart":false});
            var Q3;
            Q3=makeQuery(id+"F3.opExtrude","CAP_EDGE",EDGE,{"disambiguationData":[OSD([sQuery(id+"F2.wireOp",EDGE,"E0.right")])],"isStart":false});
            fillet(context, id + "F22", {"entities" : qUnion([Q0, Q1, Q2, Q3]), "radius" : (getVariable(context, 'radius')) * mm, "tangentPropagation" : true, "allowEdgeOverflow" : false});
        }
        {
            var Q0;
            Q0=makeQuery(id+"F3.opExtrude","CAP_EDGE",EDGE,{"disambiguationData":[OSD([sQuery(id+"F2.wireOp",EDGE,"E0.bottom")])],"isStart":true});
            var Q1;
            Q1=makeQuery(id+"F3.opExtrude","CAP_EDGE",EDGE,{"disambiguationData":[OSD([sQuery(id+"F2.wireOp",EDGE,"E0.left")])],"isStart":true});
            var Q2;
            Q2=makeQuery(id+"F3.opExtrude","CAP_EDGE",EDGE,{"disambiguationData":[OSD([sQuery(id+"F2.wireOp",EDGE,"E0.top")])],"isStart":true});
            var Q3;
            Q3=makeQuery(id+"F3.opExtrude","CAP_EDGE",EDGE,{"disambiguationData":[OSD([sQuery(id+"F2.wireOp",EDGE,"E0.right")])],"isStart":true});
            fillet(context, id + "F23", {"entities" : qUnion([Q0, Q1, Q2, Q3]), "radius" : (getVariable(context, 'radius')) * mm, "tangentPropagation" : true, "allowEdgeOverflow" : false});
        }
        {
            var Q0;
            Q0=makeQuery(id+"F3.opExtrude","SWEPT_EDGE",EDGE,{"disambiguationData":[OSD([sQuery(id+"F2.wireOp",EDGE,"E0.bottom"),sQuery(id+"F2.wireOp",EDGE,"E0.right")])]});
            var Q1;
            Q1=makeQuery(id+"F3.opExtrude","SWEPT_EDGE",EDGE,{"disambiguationData":[OSD([sQuery(id+"F2.wireOp",EDGE,"E0.bottom"),sQuery(id+"F2.wireOp",EDGE,"E0.left")])]});
            var Q2;
            Q2=makeQuery(id+"F3.opExtrude","SWEPT_EDGE",EDGE,{"disambiguationData":[OSD([sQuery(id+"F2.wireOp",EDGE,"E0.top"),sQuery(id+"F2.wireOp",EDGE,"E0.left")])]});
            var Q3;
            Q3=makeQuery(id+"F3.opExtrude","SWEPT_EDGE",EDGE,{"disambiguationData":[OSD([sQuery(id+"F2.wireOp",EDGE,"E0.top"),sQuery(id+"F2.wireOp",EDGE,"E0.right")])]});
            fillet(context, id + "F24", {"entities" : qUnion([Q0, Q1, Q2, Q3]), "radius" : (getVariable(context, 'radius')) * mm, "tangentPropagation" : true, "allowEdgeOverflow" : false});
        }
        {
            var Q0;
            Q0=qCreatedBy(makeId("Top.planeOp"),FACE);
            cPlane(context, id + "F25", {"entities" : qUnion([Q0]), "cplaneType" : CPlaneType.OFFSET, "offset" : (getVariable(context, 'size') / 2) * mm, "width" : 150 * mm, "height" : 150 * mm});
        }
        {
            var Q0;
            Q0=qCreatedBy(id+"F25.planeOp",FACE);
            var sketch = newSketch(context, id + "F26", { "sketchPlane" : qUnion([Q0])});
            skLineSegment(sketch, "E185", {"start": v(0, 12.7) * mm, "end": v(0, -12.7) * mm, "construction": true});
            skLineSegment(sketch, "E186", {"start": v(12.7, 0) * mm, "end": v(-12.7, 0) * mm, "construction": true});
            skPoint(sketch, "E186.endSnap0", {"position": v(0, 0) * mm});
            skSolve(sketch);
        }
        {
            var Q0;
            Q0=makeQuery(id+"F3.opExtrude","SWEPT_BODY",BODY,{"disambiguationData":[OSD([sQuery(id+"F2.wireOp",EDGE,"E0.bottom"),sQuery(id+"F2.wireOp",EDGE,"E0.top"),sQuery(id+"F2.wireOp",EDGE,"E0.left"),sQuery(id+"F2.wireOp",EDGE,"E0.right")])]});
            var Q1;
            Q1=sQuery(id+"F26.wireOp",EDGE,"E185");
            transform(context, id + "F27", {"entities" : qUnion([Q0]), "transformType" : TransformType.ROTATION, "transformAxis" : qUnion([Q1]), "angle" : 90 * degree, "makeCopy" : false});
        }
    });
